# Revit family: Pojemnik_na_papier_toaletowy POP S
name_source: partatom
category: Furniture
units: mm (PartAtom-declared; Revit-internal decimal feet)

## family parameters
Always vertical = Yes
Cut with Voids When Loaded = No
Host = Wall
Room Calculation Point = No
Shared = No

## types (1)
- Type 1
    Color / Kolor = White / Biały
    Depth / Glebokosc = 130 mm  [stored 0.426509 ft]
    Description = Pojemnik na papier toaletowy POP S jest naściennym dozownikiem, posiadającym ATEST PZH, wykonanym z odpornego na uszkodzenia białego plastiku ABS. Bardzo łatwo utrzymać go w czystości, co gwarantuje wysoki poziom higieny. Znajdujące się w obudowie przeźroczyste okienko umożliwia wygodne, bieżące kontrolowanie papieru w środku. Montowana wewnątrz rola może mieć średnicę w przedziale 18 - 23 cm. Ząbkowana krawędź pojemnika ułatwia odrywanie papieru, co zapewnia wysoką funkcjonalność dozownika. Jest on polecany do ogólnodostępnych toalet w szkołach, hotelach, biurach czy gabinetach lekarskich. Dzięki uniwersalnemu designowi i atrakcyjnej cenie jest jednym z najczęściej wybieranych modeli pojemników na papier toaletowy. Jest to doskonały podajnik papieru do każdej toalety publicznej.
    Height / Wysokosc = 260 mm  [stored 0.853018 ft]
    Manufacturer = FANECO.com
    Manufacturer code / Kod producenta = 5901764290124
    Material finish / Wykonczenie = Plastic ABS
    Model = POP S
    Product code / Kod produktu = J18PGWG
    URL = https://faneco.com
    Weight / Waga = 0.6 kg
    Width / Szerokosc = 240 mm  [stored 0.787402 ft]

note: [stored X ft] marks values corroborated as IEEE doubles in the binary element streams (Revit-internal decimal feet)

## geometry (parser evidence)
native form markers: Blend x4, Sweep x10
no freeform markers — native parametric forms only
